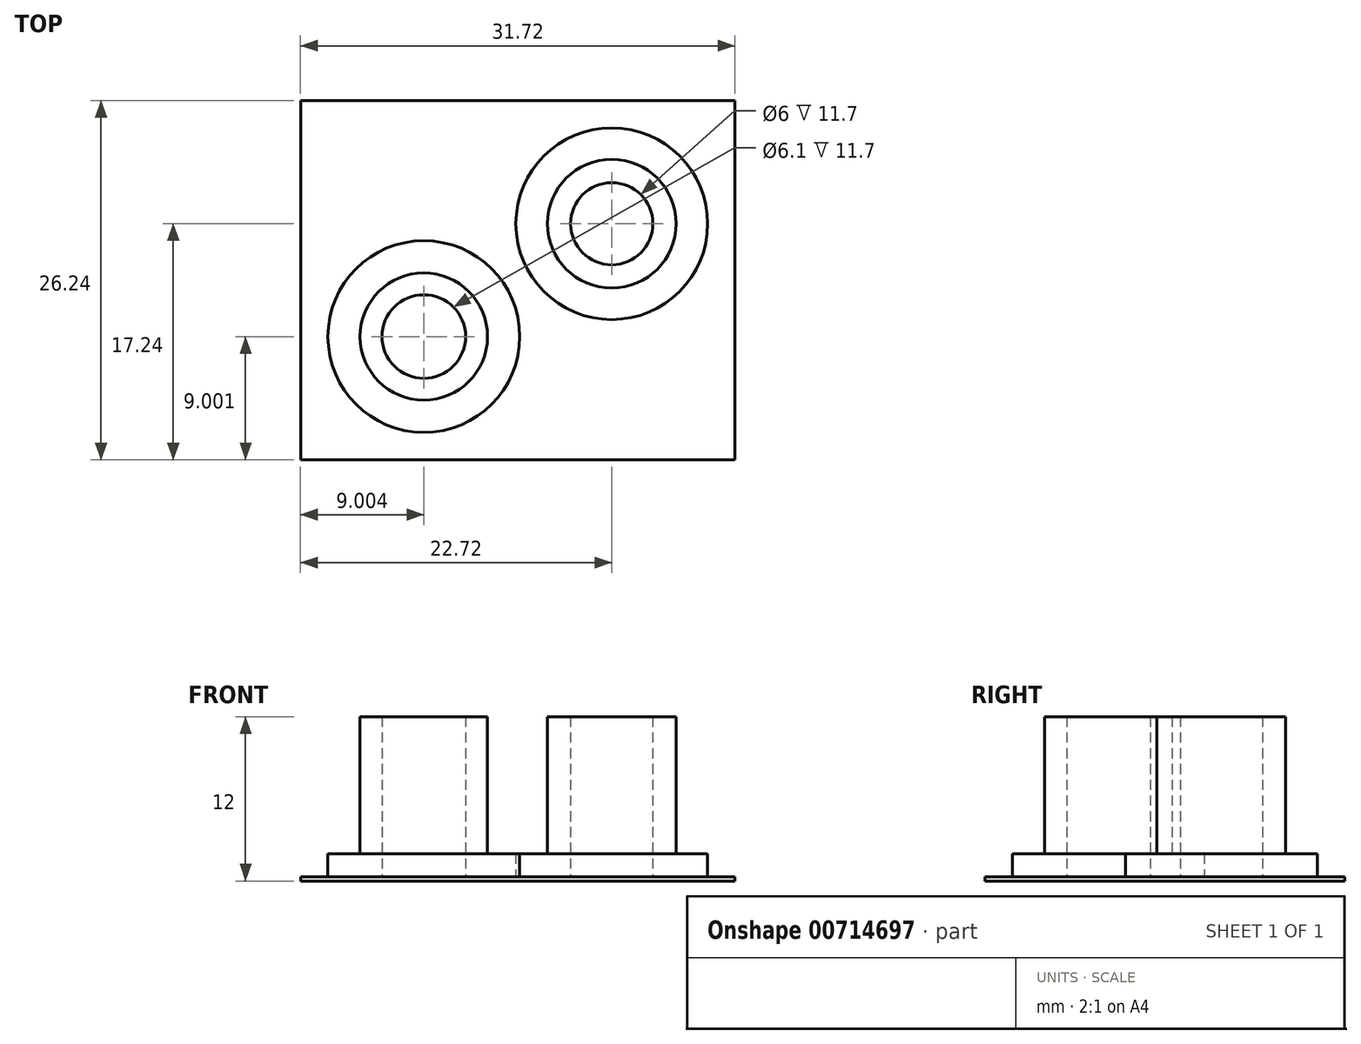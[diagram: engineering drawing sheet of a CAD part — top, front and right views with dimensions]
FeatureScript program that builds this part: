
annotation { "Feature Type Name" : "Feature", "Feature Type Description" : "" }
export const myFeature = defineFeature(function(context is Context, id is Id, definition is map)
    precondition{}
    {
        {
            var Q0;
            Q0=qCreatedBy(makeId("Top.planeOp"),FACE);
            var sketch = newSketch(context, id + "F0", { "sketchPlane" : qUnion([Q0])});
            skCircle(sketch, "E0", {"center": v(0, 0) * mm, "radius": 7 * mm});
            skCircle(sketch, "E1", {"center": v(0, 0) * mm, "radius": 4.7 * mm});
            skCircle(sketch, "E2", {"center": v(0, 0) * mm, "radius": 3 * mm});
            skCircle(sketch, "E3", {"center": v(-13.72, -8.24) * mm, "radius": 3.05 * mm});
            skCircle(sketch, "E4", {"center": v(-13.72, -8.24) * mm, "radius": 4.65 * mm});
            skCircle(sketch, "E5", {"center": v(-13.72, -8.24) * mm, "radius": 7 * mm});
            skLineSegment(sketch, "E6.bottom", {"start": v(-22.72, 9) * mm, "end": v(9, 9) * mm});
            skLineSegment(sketch, "E6.top", {"start": v(-22.72, -17.24) * mm, "end": v(9, -17.24) * mm});
            skLineSegment(sketch, "E6.left", {"start": v(-22.72, 9) * mm, "end": v(-22.72, -17.24) * mm});
            skLineSegment(sketch, "E6.right", {"start": v(9, 9) * mm, "end": v(9, -17.24) * mm});
            skSolve(sketch);
        }
        {
            var Q0;
            Q0=makeQuery(id+"F0.imprint","IMPRINT",FACE,{"disambiguationData":[TD([[makeQuery(id+"F0.imprint","IMPRINT",EDGE,{"derivedFrom":sQuery(id+"F0.wireOp",EDGE,"E1")}),1.0]])]});
            var Q1;
            Q1=makeQuery(id+"F0.imprint","IMPRINT",FACE,{"disambiguationData":[TD([[makeQuery(id+"F0.imprint","IMPRINT",EDGE,{"derivedFrom":sQuery(id+"F0.wireOp",EDGE,"E0")}),1.0]])]});
            extrude(context, id + "F1", {"entities" : qUnion([Q0, Q1]), "depth" : 2 * mm, "offsetDistance" : 25 * mm});
        }
        {
            var Q0;
            Q0=makeQuery(id+"F0.imprint","IMPRINT",FACE,{"disambiguationData":[TD([[makeQuery(id+"F0.imprint","IMPRINT",EDGE,{"derivedFrom":sQuery(id+"F0.wireOp",EDGE,"E1")}),1.0]])]});
            extrude(context, id + "F2", {"entities" : qUnion([Q0]), "operationType" : NewBodyOperationType.ADD, "depth" : 12 * mm, "offsetDistance" : 25 * mm});
        }
        {
            var Q0;
            Q0=makeQuery(id+"F0.imprint","IMPRINT",FACE,{"disambiguationData":[TD([[makeQuery(id+"F0.imprint","IMPRINT",EDGE,{"derivedFrom":sQuery(id+"F0.wireOp",EDGE,"E4")}),-1.0]])]});
            extrude(context, id + "F3", {"entities" : qUnion([Q0]), "depth" : 2 * mm, "offsetDistance" : 25 * mm});
        }
        {
            var Q0;
            Q0=makeQuery(id+"F0.imprint","IMPRINT",FACE,{"disambiguationData":[TD([[makeQuery(id+"F0.imprint","IMPRINT",EDGE,{"derivedFrom":sQuery(id+"F0.wireOp",EDGE,"E3")}),-1.0]])]});
            extrude(context, id + "F4", {"entities" : qUnion([Q0]), "operationType" : NewBodyOperationType.ADD, "depth" : 12 * mm, "offsetDistance" : 25 * mm});
        }
        {
            var Q0;
            Q0=makeQuery(id+"F0.imprint","IMPRINT",FACE,{"disambiguationData":[TD([[makeQuery(id+"F0.imprint","IMPRINT",EDGE,{"derivedFrom":sQuery(id+"F0.wireOp",EDGE,"E0")}),-1.0]])]});
            var Q1;
            Q1=makeQuery(id+"F0.imprint","IMPRINT",FACE,{"disambiguationData":[TD([[makeQuery(id+"F0.imprint","IMPRINT",EDGE,{"derivedFrom":sQuery(id+"F0.wireOp",EDGE,"E4")}),-1.0]])]});
            var Q2;
            Q2=makeQuery(id+"F0.imprint","IMPRINT",FACE,{"disambiguationData":[TD([[makeQuery(id+"F0.imprint","IMPRINT",EDGE,{"derivedFrom":sQuery(id+"F0.wireOp",EDGE,"E3")}),-1.0]])]});
            var Q3;
            Q3=makeQuery(id+"F0.imprint","IMPRINT",FACE,{"disambiguationData":[TD([[makeQuery(id+"F0.imprint","IMPRINT",EDGE,{"derivedFrom":sQuery(id+"F0.wireOp",EDGE,"E3")}),1.0]])]});
            var Q4;
            Q4=makeQuery(id+"F0.imprint","IMPRINT",FACE,{"disambiguationData":[TD([[makeQuery(id+"F0.imprint","IMPRINT",EDGE,{"derivedFrom":sQuery(id+"F0.wireOp",EDGE,"E2")}),1.0]])]});
            var Q5;
            Q5=makeQuery(id+"F0.imprint","IMPRINT",FACE,{"disambiguationData":[TD([[makeQuery(id+"F0.imprint","IMPRINT",EDGE,{"derivedFrom":sQuery(id+"F0.wireOp",EDGE,"E1")}),1.0]])]});
            var Q6;
            Q6=makeQuery(id+"F0.imprint","IMPRINT",FACE,{"disambiguationData":[TD([[makeQuery(id+"F0.imprint","IMPRINT",EDGE,{"derivedFrom":sQuery(id+"F0.wireOp",EDGE,"E0")}),1.0]])]});
            extrude(context, id + "F5", {"entities" : qUnion([Q0, Q1, Q2, Q3, Q4, Q5, Q6]), "operationType" : NewBodyOperationType.ADD, "depth" : .3 * mm, "offsetDistance" : 25 * mm});
        }
    });
